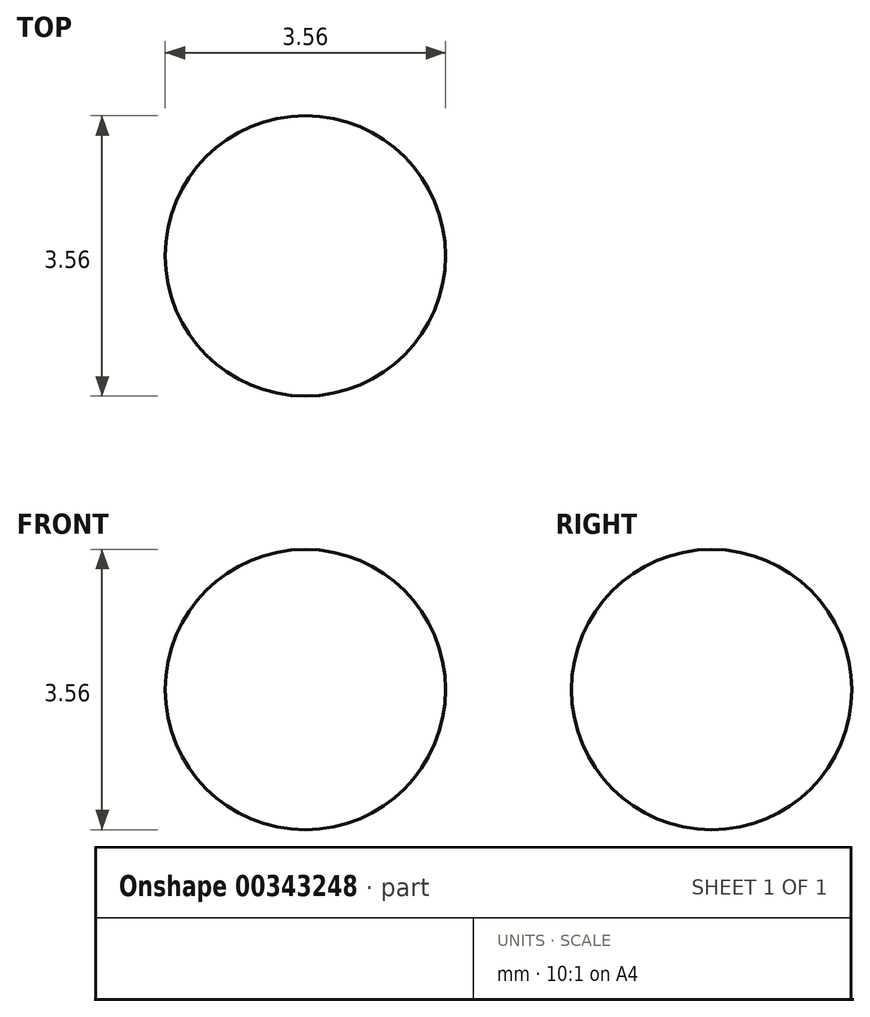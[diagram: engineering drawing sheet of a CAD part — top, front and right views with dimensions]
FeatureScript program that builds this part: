
annotation { "Feature Type Name" : "Feature", "Feature Type Description" : "" }
export const myFeature = defineFeature(function(context is Context, id is Id, definition is map)
    precondition{}
    {
        {
            var Q0;
            Q0=qCreatedBy(makeId("Front.planeOp"),FACE);
            var sketch = newSketch(context, id + "F0", { "sketchPlane" : qUnion([Q0])});
            skLineSegment(sketch, "E0", {"start": v(0, 0) * mm, "end": v(0, 3.56) * mm});
            skArc(sketch, "E1", {"start": v(0, 3.56) * mm, "mid": v(-1.78, 1.78) * mm, "end": v(0, 0) * mm});
            skSolve(sketch);
        }
        {
            var Q0;
            Q0=makeQuery(id+"F0.imprint","IMPRINT",FACE,{"disambiguationData":[TD([[makeQuery(id+"F0.imprint","IMPRINT",EDGE,{"derivedFrom":sQuery(id+"F0.wireOp",EDGE,"E0")}),1.0]])]});
            var Q1;
            Q1=sQuery(id+"F0.wireOp",EDGE,"E0");
            revolve(context, id + "F1", {"entities" : qUnion([Q0]), "axis" : qUnion([Q1]), "revolveType" : RevolveType.FULL});
        }
    });
